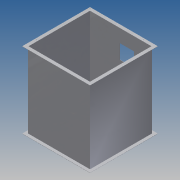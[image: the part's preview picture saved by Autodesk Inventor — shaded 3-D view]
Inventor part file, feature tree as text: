
AUTODESK INVENTOR PART (.ipt)
format: ipt  version: 2014 SP1 (Build 180222100, 222)  size: 163,840 bytes
history: native  units: in
note: dims shown in document units (in); Inventor stores cm internally (conversion verified against a paired STEP export)
features: sketch x8, extrude x7, hole x1, other x1
ambient origin geometry x8: Origin, YZ Plane, XZ Plane, XY Plane, X Axis, Y Axis, Z Axis, Center Point
bodies: Solid1 (feature_tree)
feature tree (17):
  extrude  "Extrusion1"  Depth=33.4646in
  extrude  "Extrusion2"  Depth=1.5748in
  extrude  "Extrusion3"  Depth=0.1in
  extrude  "Extrusion4"  Depth=1.4764in TaperAngle=0.0deg
  extrude  "Extrusion5"  Depth=0.1in
  hole  "Hole1"  [1 undecoded]
  extrude  "Extrusion6"  Depth=1.4764in TaperAngle=0.0deg
  extrude  "Extrusion8"  Depth=1.0in
  other  "Power"
  sketch  "Sketch1"  dims[d0=33.4646in d1=33.4646in]
  sketch  "Sketch2"  dims[d2=37.4016in d3=0.0in d4=1.5748in]
  sketch  "Sketch3"  dims[d5=39.3701in d6=0.0in d7=0.1in]
  sketch  "Sketch4"  dims[d8=0.1in d9=1.4764in d10=0.0in]
  sketch  "Sketch5"  dims[d11=0.1in d12=0.1in]
  sketch  "Sketch6"  dims[d13=1.4764in d14=0.0in d15=1.4764in]
  sketch  "Sketch7"  dims[d16=1.4764in d17=39.3701in d18=0.0in]
  sketch  "Sketch9"  dims[d19=0.5906in d20=0.5906in d21=0.7874in d23=26.378in d24=0.7874in d26=26.378in d29=0.25in d30=0.75in d31=0.375in d32=0.25in d33=0.5635in d34=1.0in d35=0.8108in d36=8.6614in d37=7.0866in d38=7.0866in d39=0.3937in d40=0.0in d48=1.5in d49=2.0in d50=1.0in d51=0.0in]
note: 1 required parameter value undecoded (feature->parameter linkage not recoverable at this tier; creation-order binding heuristic only, values carry confidence <= 0.55)
